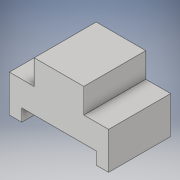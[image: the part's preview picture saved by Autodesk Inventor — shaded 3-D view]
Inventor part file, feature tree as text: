
AUTODESK INVENTOR PART (.ipt)
format: ipt  version: 2018 (Build 220112000, 112)  size: 105,472 bytes
history: native  units: in
note: dims shown in document units (in); Inventor stores cm internally (conversion verified against a paired STEP export)
features: extrude x1, sketch x1
ambient origin geometry x8: Origin, YZ Plane, XZ Plane, XY Plane, X Axis, Y Axis, Z Axis, Center Point
bodies: Solid1 (feature_tree)
feature tree (2):
  extrude  "Extrusion1"  Depth=0.25in
  sketch  "Sketch1"  dims[d0=0.25in d1=0.25in d2=1.5in d3=0.25in d4=0.75in d5=0.5in d6=0.5in d7=1.0in d8=0.5in d9=1.25in d10=0.0in]
